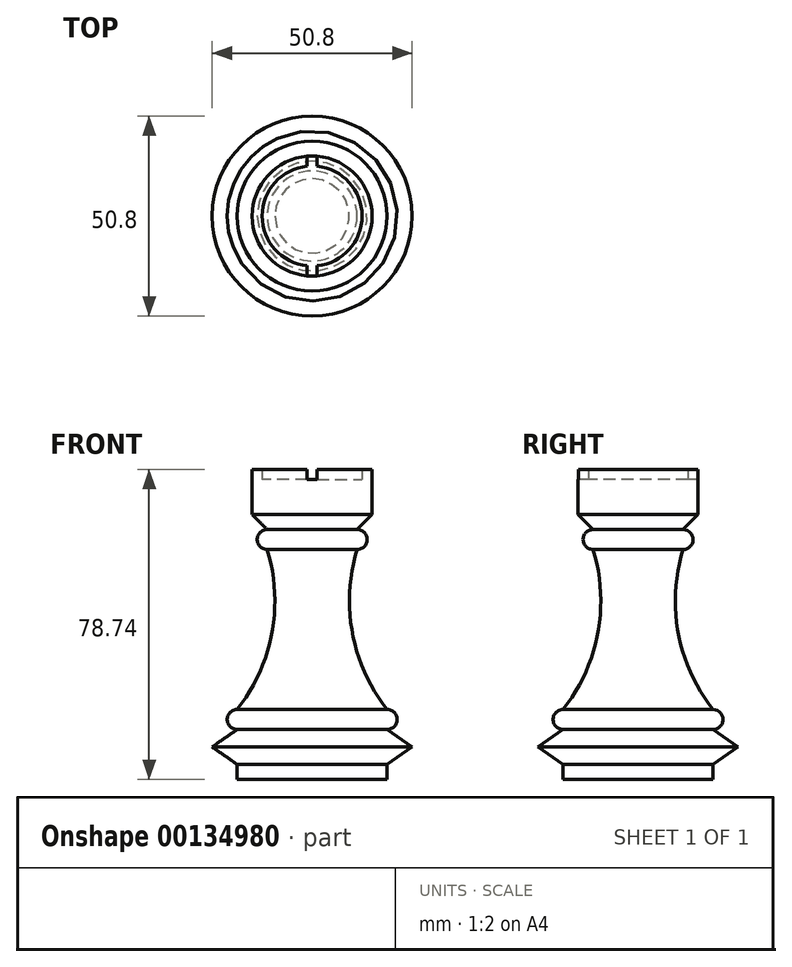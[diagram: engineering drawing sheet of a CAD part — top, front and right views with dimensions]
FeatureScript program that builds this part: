
annotation { "Feature Type Name" : "Feature", "Feature Type Description" : "" }
export const myFeature = defineFeature(function(context is Context, id is Id, definition is map)
    precondition{}
    {
        {
            var Q0;
            Q0=qCreatedBy(makeId("Front.planeOp"),FACE);
            var sketch = newSketch(context, id + "F0", { "sketchPlane" : qUnion([Q0])});
            skLineSegment(sketch, "E0", {"start": v(0, 0) * mm, "end": v(19.05, 0) * mm});
            skLineSegment(sketch, "E1", {"start": v(19.05, 0) * mm, "end": v(19.05, 3.8) * mm});
            skLineSegment(sketch, "E2", {"start": v(19.05, 3.81) * mm, "end": v(25.4, 8.26) * mm});
            skLineSegment(sketch, "E3", {"start": v(25.4, 8.25) * mm, "end": v(19.05, 12.7) * mm});
            skLineSegment(sketch, "E4", {"start": v(0, 0) * mm, "end": v(0, 76.2) * mm});
            skLineSegment(sketch, "E5", {"start": v(0, 76.2) * mm, "end": v(12.7, 76.2) * mm});
            skLineSegment(sketch, "E6", {"start": v(12.7, 76.2) * mm, "end": v(12.7, 78.74) * mm});
            skLineSegment(sketch, "E7", {"start": v(12.7, 78.74) * mm, "end": v(15.24, 78.74) * mm});
            skLineSegment(sketch, "E8", {"start": v(15.24, 78.74) * mm, "end": v(15.24, 67.31) * mm});
            skLineSegment(sketch, "E9", {"start": v(15.24, 67.31) * mm, "end": v(11.43, 63.5) * mm});
            skArc(sketch, "E10", {"start": v(11.43, 58.42) * mm, "mid": v(13.97, 60.96) * mm, "end": v(11.43, 63.5) * mm});
            skArc(sketch, "E11", {"start": v(19.05, 12.7) * mm, "mid": v(21.59, 15.24) * mm, "end": v(19.05, 17.78) * mm});
            skArc(sketch, "E12", {"start": v(11.43, 58.42) * mm, "mid": v(10.23, 37.16) * mm, "end": v(19.05, 17.78) * mm});
            skSolve(sketch);
        }
        {
            var Q0;
            Q0 = qSketchRegion(id + "F0", true);
            var Q1;
            Q1=sQuery(id+"F0.wireOp",EDGE,"E4");
            revolve(context, id + "F1", {"entities" : qUnion([Q0]), "axis" : qUnion([Q1]), "revolveType" : RevolveType.FULL});
        }
        {
            var Q0;
            Q0=qCreatedBy(makeId("Front.planeOp"),FACE);
            var sketch = newSketch(context, id + "F2", { "sketchPlane" : qUnion([Q0])});
            skLineSegment(sketch, "E13.bottom", {"start": v(1.27, 78.74) * mm, "end": v(-1.27, 78.74) * mm});
            skLineSegment(sketch, "E13.top", {"start": v(1.27, 76.2) * mm, "end": v(-1.27, 76.2) * mm});
            skLineSegment(sketch, "E13.left", {"start": v(1.27, 78.74) * mm, "end": v(1.27, 76.2) * mm});
            skLineSegment(sketch, "E13.right", {"start": v(-1.27, 78.74) * mm, "end": v(-1.27, 76.2) * mm});
            skPoint(sketch, "E13.middle", {"position": v(0, 77.47) * mm});
            skSolve(sketch);
        }
        {
            var Q0;
            Q0 = qSketchRegion(id + "F2", true);
            extrude(context, id + "F3", {"entities" : qUnion([Q0]), "operationType" : NewBodyOperationType.REMOVE, "endBound" : BoundingType.THROUGH_ALL, "oppositeDirection" : true, "depth" : 25.4 * mm, "hasSecondDirection" : true, "secondDirectionBound" : SecondDirectionBoundingType.THROUGH_ALL, "secondDirectionOppositeDirection" : false, "secondDirectionDepth" : 25.4 * mm});
        }
    });
